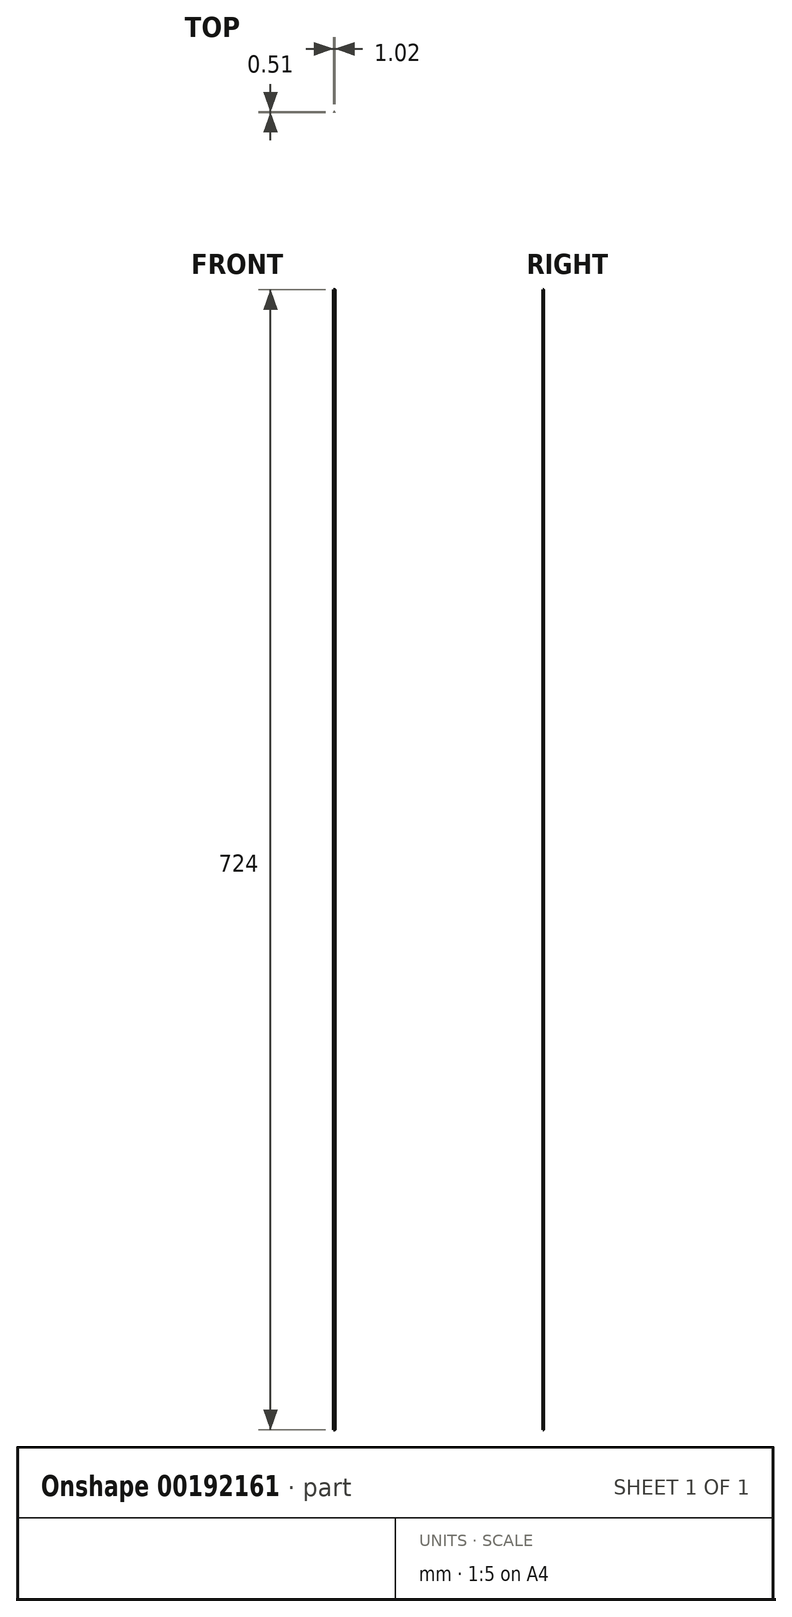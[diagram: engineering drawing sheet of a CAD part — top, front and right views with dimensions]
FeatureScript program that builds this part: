
annotation { "Feature Type Name" : "Feature", "Feature Type Description" : "" }
export const myFeature = defineFeature(function(context is Context, id is Id, definition is map)
    precondition{}
    {
        {
            var Q0;
            Q0=qCreatedBy(makeId("Top.planeOp"),FACE);
            var sketch = newSketch(context, id + "F0", { "sketchPlane" : qUnion([Q0])});
            skLineSegment(sketch, "E0.0", {"start": v(-8.74, 7.13) * mm, "end": v(-5.44, 3.84) * mm});
            skPoint(sketch, "E1.0", {"position": v(-9.86, 7.35) * mm});
            skArc(sketch, "E2.0", {"start": v(-10.5, 6.4) * mm, "mid": v(-9.86, 7.35) * mm, "end": v(-8.74, 7.13) * mm});
            skLineSegment(sketch, "E3.0", {"start": v(-10.5, 4.29) * mm, "end": v(-10.5, 6.4) * mm});
            skArc(sketch, "E4.0", {"start": v(-11.54, 3.24) * mm, "mid": v(-10.8, 3.55) * mm, "end": v(-10.5, 4.29) * mm});
            skArc(sketch, "E5.0.0", {"start": v(-3.95, -5.42) * mm, "mid": v(-2.92, -4.74) * mm, "end": v(-1.7, -4.5) * mm});
            skLineSegment(sketch, "E5.0.1", {"start": v(-1.7, -4.5) * mm, "end": v(1.7, -4.5) * mm});
            skArc(sketch, "E5.0.2", {"start": v(1.7, -4.5) * mm, "mid": v(2.92, -4.74) * mm, "end": v(3.95, -5.42) * mm});
            skLineSegment(sketch, "E5.0.3", {"start": v(3.95, -5.42) * mm, "end": v(7.18, -8.65) * mm});
            skArc(sketch, "E5.0.4", {"start": v(7.18, -8.65) * mm, "mid": v(7.41, -9.82) * mm, "end": v(6.42, -10.5) * mm});
            skLineSegment(sketch, "E5.0.5", {"start": v(6.42, -10.5) * mm, "end": v(4.29, -10.5) * mm});
            skArc(sketch, "E5.0.6", {"start": v(4.29, -10.5) * mm, "mid": v(3.55, -10.8) * mm, "end": v(3.24, -11.54) * mm});
            skLineSegment(sketch, "E5.0.7", {"start": v(3.24, -11.54) * mm, "end": v(3.24, -11.65) * mm});
            skArc(sketch, "E5.0.8", {"start": v(3.24, -11.65) * mm, "mid": v(3.55, -12.4) * mm, "end": v(4.29, -12.7) * mm});
            skLineSegment(sketch, "E5.0.9", {"start": v(4.29, -12.7) * mm, "end": v(5.32, -12.7) * mm});
            skArc(sketch, "E5.0.10", {"start": v(5.32, -12.7) * mm, "mid": v(5.83, -12.2) * mm, "end": v(6.33, -12.7) * mm});
            skLineSegment(sketch, "E5.0.11", {"start": v(6.33, -12.7) * mm, "end": v(9.55, -12.7) * mm});
            skArc(sketch, "E5.0.12", {"start": v(9.55, -12.7) * mm, "mid": v(10.06, -12.2) * mm, "end": v(10.57, -12.7) * mm});
            skArc(sketch, "E5.0.13", {"start": v(10.57, -12.7) * mm, "mid": v(12.08, -12.08) * mm, "end": v(12.7, -10.57) * mm});
            skArc(sketch, "E5.0.14", {"start": v(12.7, -10.57) * mm, "mid": v(12.2, -10.06) * mm, "end": v(12.7, -9.55) * mm});
            skLineSegment(sketch, "E5.0.15", {"start": v(12.7, -9.55) * mm, "end": v(12.7, -6.33) * mm});
            skArc(sketch, "E5.0.16", {"start": v(12.7, -6.33) * mm, "mid": v(12.2, -5.83) * mm, "end": v(12.7, -5.32) * mm});
            skLineSegment(sketch, "E5.0.17", {"start": v(12.7, -5.32) * mm, "end": v(12.7, -4.29) * mm});
            skArc(sketch, "E5.0.18", {"start": v(12.7, -4.29) * mm, "mid": v(12.4, -3.55) * mm, "end": v(11.65, -3.24) * mm});
            skLineSegment(sketch, "E5.0.19", {"start": v(11.65, -3.24) * mm, "end": v(11.54, -3.24) * mm});
            skArc(sketch, "E5.0.20", {"start": v(11.54, -3.24) * mm, "mid": v(10.8, -3.55) * mm, "end": v(10.5, -4.29) * mm});
            skLineSegment(sketch, "E5.0.21", {"start": v(10.5, -4.29) * mm, "end": v(10.5, -6.4) * mm});
            skArc(sketch, "E5.0.22", {"start": v(10.5, -6.4) * mm, "mid": v(9.86, -7.35) * mm, "end": v(8.74, -7.13) * mm});
            skLineSegment(sketch, "E5.0.23", {"start": v(8.74, -7.13) * mm, "end": v(5.44, -3.84) * mm});
            skArc(sketch, "E5.0.24", {"start": v(5.44, -3.84) * mm, "mid": v(4.75, -2.8) * mm, "end": v(4.5, -1.6) * mm});
            skLineSegment(sketch, "E5.0.25", {"start": v(4.5, -1.6) * mm, "end": v(4.5, 1.6) * mm});
            skArc(sketch, "E5.0.26", {"start": v(4.5, 1.6) * mm, "mid": v(4.75, 2.8) * mm, "end": v(5.44, 3.84) * mm});
            skLineSegment(sketch, "E5.0.27", {"start": v(5.44, 3.84) * mm, "end": v(8.74, 7.13) * mm});
            skArc(sketch, "E5.0.28", {"start": v(8.74, 7.13) * mm, "mid": v(9.86, 7.35) * mm, "end": v(10.5, 6.4) * mm});
            skLineSegment(sketch, "E5.0.29", {"start": v(10.5, 6.4) * mm, "end": v(10.5, 4.29) * mm});
            skArc(sketch, "E5.0.30", {"start": v(10.5, 4.29) * mm, "mid": v(10.8, 3.55) * mm, "end": v(11.54, 3.24) * mm});
            skLineSegment(sketch, "E5.0.31", {"start": v(11.54, 3.24) * mm, "end": v(11.65, 3.24) * mm});
            skArc(sketch, "E5.0.32", {"start": v(11.65, 3.24) * mm, "mid": v(12.4, 3.55) * mm, "end": v(12.7, 4.29) * mm});
            skLineSegment(sketch, "E5.0.33", {"start": v(12.7, 4.29) * mm, "end": v(12.7, 5.32) * mm});
            skArc(sketch, "E5.0.34", {"start": v(12.7, 5.32) * mm, "mid": v(12.2, 5.83) * mm, "end": v(12.7, 6.33) * mm});
            skLineSegment(sketch, "E5.0.35", {"start": v(12.7, 6.33) * mm, "end": v(12.7, 9.55) * mm});
            skArc(sketch, "E5.0.36", {"start": v(12.7, 9.55) * mm, "mid": v(12.2, 10.06) * mm, "end": v(12.7, 10.57) * mm});
            skArc(sketch, "E5.0.37", {"start": v(12.7, 10.57) * mm, "mid": v(12.08, 12.08) * mm, "end": v(10.57, 12.7) * mm});
            skArc(sketch, "E5.0.38", {"start": v(10.57, 12.7) * mm, "mid": v(10.06, 12.2) * mm, "end": v(9.55, 12.7) * mm});
            skLineSegment(sketch, "E5.0.39", {"start": v(9.55, 12.7) * mm, "end": v(6.33, 12.7) * mm});
            skArc(sketch, "E5.0.40", {"start": v(6.33, 12.7) * mm, "mid": v(5.83, 12.2) * mm, "end": v(5.32, 12.7) * mm});
            skLineSegment(sketch, "E5.0.41", {"start": v(5.32, 12.7) * mm, "end": v(4.29, 12.7) * mm});
            skArc(sketch, "E5.0.42", {"start": v(4.29, 12.7) * mm, "mid": v(3.55, 12.4) * mm, "end": v(3.24, 11.65) * mm});
            skLineSegment(sketch, "E5.0.43", {"start": v(3.24, 11.65) * mm, "end": v(3.24, 11.54) * mm});
            skArc(sketch, "E5.0.44", {"start": v(3.24, 11.54) * mm, "mid": v(3.55, 10.8) * mm, "end": v(4.29, 10.5) * mm});
            skLineSegment(sketch, "E5.0.45", {"start": v(4.29, 10.5) * mm, "end": v(6.48, 10.5) * mm});
            skArc(sketch, "E5.0.46", {"start": v(6.48, 10.5) * mm, "mid": v(7.43, 9.85) * mm, "end": v(7.2, 8.72) * mm});
            skLineSegment(sketch, "E5.0.47", {"start": v(7.2, 8.72) * mm, "end": v(3.9, 5.42) * mm});
            skArc(sketch, "E5.0.48", {"start": v(3.9, 5.42) * mm, "mid": v(2.87, 4.74) * mm, "end": v(1.66, 4.5) * mm});
            skLineSegment(sketch, "E5.0.49", {"start": v(1.66, 4.5) * mm, "end": v(-1.66, 4.5) * mm});
            skArc(sketch, "E5.0.50", {"start": v(-1.66, 4.5) * mm, "mid": v(-2.87, 4.74) * mm, "end": v(-3.9, 5.42) * mm});
            skLineSegment(sketch, "E5.0.51", {"start": v(-3.9, 5.42) * mm, "end": v(-7.2, 8.72) * mm});
            skArc(sketch, "E5.0.52", {"start": v(-7.2, 8.72) * mm, "mid": v(-7.43, 9.85) * mm, "end": v(-6.48, 10.5) * mm});
            skLineSegment(sketch, "E5.0.53", {"start": v(-6.48, 10.5) * mm, "end": v(-4.29, 10.5) * mm});
            skArc(sketch, "E5.0.54", {"start": v(-4.29, 10.5) * mm, "mid": v(-3.55, 10.8) * mm, "end": v(-3.24, 11.54) * mm});
            skLineSegment(sketch, "E5.0.55", {"start": v(-3.24, 11.54) * mm, "end": v(-3.24, 11.65) * mm});
            skArc(sketch, "E5.0.56", {"start": v(-3.24, 11.65) * mm, "mid": v(-3.55, 12.4) * mm, "end": v(-4.29, 12.7) * mm});
            skLineSegment(sketch, "E5.0.57", {"start": v(-4.29, 12.7) * mm, "end": v(-5.32, 12.7) * mm});
            skArc(sketch, "E5.0.58", {"start": v(-5.32, 12.7) * mm, "mid": v(-5.83, 12.2) * mm, "end": v(-6.33, 12.7) * mm});
            skLineSegment(sketch, "E5.0.59", {"start": v(-6.33, 12.7) * mm, "end": v(-9.55, 12.7) * mm});
            skArc(sketch, "E5.0.60", {"start": v(-9.55, 12.7) * mm, "mid": v(-10.06, 12.2) * mm, "end": v(-10.57, 12.7) * mm});
            skArc(sketch, "E5.0.61", {"start": v(-10.57, 12.7) * mm, "mid": v(-12.08, 12.08) * mm, "end": v(-12.7, 10.57) * mm});
            skArc(sketch, "E5.0.62", {"start": v(-12.7, 10.57) * mm, "mid": v(-12.2, 10.06) * mm, "end": v(-12.7, 9.55) * mm});
            skLineSegment(sketch, "E5.0.63", {"start": v(-12.7, 9.55) * mm, "end": v(-12.7, 6.33) * mm});
            skArc(sketch, "E5.0.64", {"start": v(-12.7, 6.33) * mm, "mid": v(-12.2, 5.83) * mm, "end": v(-12.7, 5.32) * mm});
            skLineSegment(sketch, "E5.0.65", {"start": v(-12.7, 5.32) * mm, "end": v(-12.7, 4.29) * mm});
            skArc(sketch, "E5.0.66", {"start": v(-12.7, 4.29) * mm, "mid": v(-12.4, 3.55) * mm, "end": v(-11.65, 3.24) * mm});
            skLineSegment(sketch, "E5.0.67", {"start": v(-11.65, 3.24) * mm, "end": v(-11.54, 3.24) * mm});
            skArc(sketch, "E5.0.72", {"start": v(-5.44, 3.84) * mm, "mid": v(-4.75, 2.8) * mm, "end": v(-4.5, 1.6) * mm});
            skLineSegment(sketch, "E5.0.73", {"start": v(-4.5, 1.6) * mm, "end": v(-4.5, -1.6) * mm});
            skArc(sketch, "E5.0.74", {"start": v(-4.5, -1.6) * mm, "mid": v(-4.75, -2.8) * mm, "end": v(-5.44, -3.84) * mm});
            skLineSegment(sketch, "E5.0.75", {"start": v(-5.44, -3.84) * mm, "end": v(-8.74, -7.13) * mm});
            skArc(sketch, "E5.0.76", {"start": v(-8.74, -7.13) * mm, "mid": v(-9.86, -7.35) * mm, "end": v(-10.5, -6.4) * mm});
            skLineSegment(sketch, "E5.0.77", {"start": v(-10.5, -6.4) * mm, "end": v(-10.5, -4.29) * mm});
            skArc(sketch, "E5.0.78", {"start": v(-10.5, -4.29) * mm, "mid": v(-10.8, -3.55) * mm, "end": v(-11.54, -3.24) * mm});
            skLineSegment(sketch, "E5.0.79", {"start": v(-11.54, -3.24) * mm, "end": v(-11.65, -3.24) * mm});
            skArc(sketch, "E5.0.80", {"start": v(-11.65, -3.24) * mm, "mid": v(-12.4, -3.55) * mm, "end": v(-12.7, -4.29) * mm});
            skLineSegment(sketch, "E5.0.81", {"start": v(-12.7, -4.29) * mm, "end": v(-12.7, -5.32) * mm});
            skArc(sketch, "E5.0.82", {"start": v(-12.7, -5.32) * mm, "mid": v(-12.2, -5.83) * mm, "end": v(-12.7, -6.33) * mm});
            skLineSegment(sketch, "E5.0.83", {"start": v(-12.7, -6.33) * mm, "end": v(-12.7, -9.55) * mm});
            skArc(sketch, "E5.0.84", {"start": v(-12.7, -9.55) * mm, "mid": v(-12.2, -10.06) * mm, "end": v(-12.7, -10.57) * mm});
            skArc(sketch, "E5.0.85", {"start": v(-12.7, -10.57) * mm, "mid": v(-12.08, -12.08) * mm, "end": v(-10.57, -12.7) * mm});
            skArc(sketch, "E5.0.86", {"start": v(-10.57, -12.7) * mm, "mid": v(-10.06, -12.2) * mm, "end": v(-9.55, -12.7) * mm});
            skLineSegment(sketch, "E5.0.87", {"start": v(-9.55, -12.7) * mm, "end": v(-6.33, -12.7) * mm});
            skArc(sketch, "E5.0.88", {"start": v(-6.33, -12.7) * mm, "mid": v(-5.83, -12.2) * mm, "end": v(-5.32, -12.7) * mm});
            skLineSegment(sketch, "E5.0.89", {"start": v(-5.32, -12.7) * mm, "end": v(-4.29, -12.7) * mm});
            skArc(sketch, "E5.0.90", {"start": v(-4.29, -12.7) * mm, "mid": v(-3.55, -12.4) * mm, "end": v(-3.24, -11.65) * mm});
            skLineSegment(sketch, "E5.0.91", {"start": v(-3.24, -11.65) * mm, "end": v(-3.24, -11.54) * mm});
            skArc(sketch, "E5.0.92", {"start": v(-3.24, -11.54) * mm, "mid": v(-3.55, -10.8) * mm, "end": v(-4.29, -10.5) * mm});
            skLineSegment(sketch, "E5.0.93", {"start": v(-4.29, -10.5) * mm, "end": v(-6.42, -10.5) * mm});
            skArc(sketch, "E5.0.94", {"start": v(-6.42, -10.5) * mm, "mid": v(-7.41, -9.82) * mm, "end": v(-7.18, -8.65) * mm});
            skLineSegment(sketch, "E5.0.95", {"start": v(-7.18, -8.65) * mm, "end": v(-3.95, -5.42) * mm});
            skSolve(sketch);
        }
        {
            var Q0;
            Q0=makeQuery(id+"F0.imprint","IMPRINT",FACE,{"disambiguationData":[TD([[makeQuery(id+"F0.imprint","IMPRINT",EDGE,{"derivedFrom":sQuery(id+"F0.wireOp",EDGE,"E5.0.12")}),1.0]])]});
            extrude(context, id + "F1", {"entities" : qUnion([Q0]), "depth" : 724 * mm});
        }
    });
